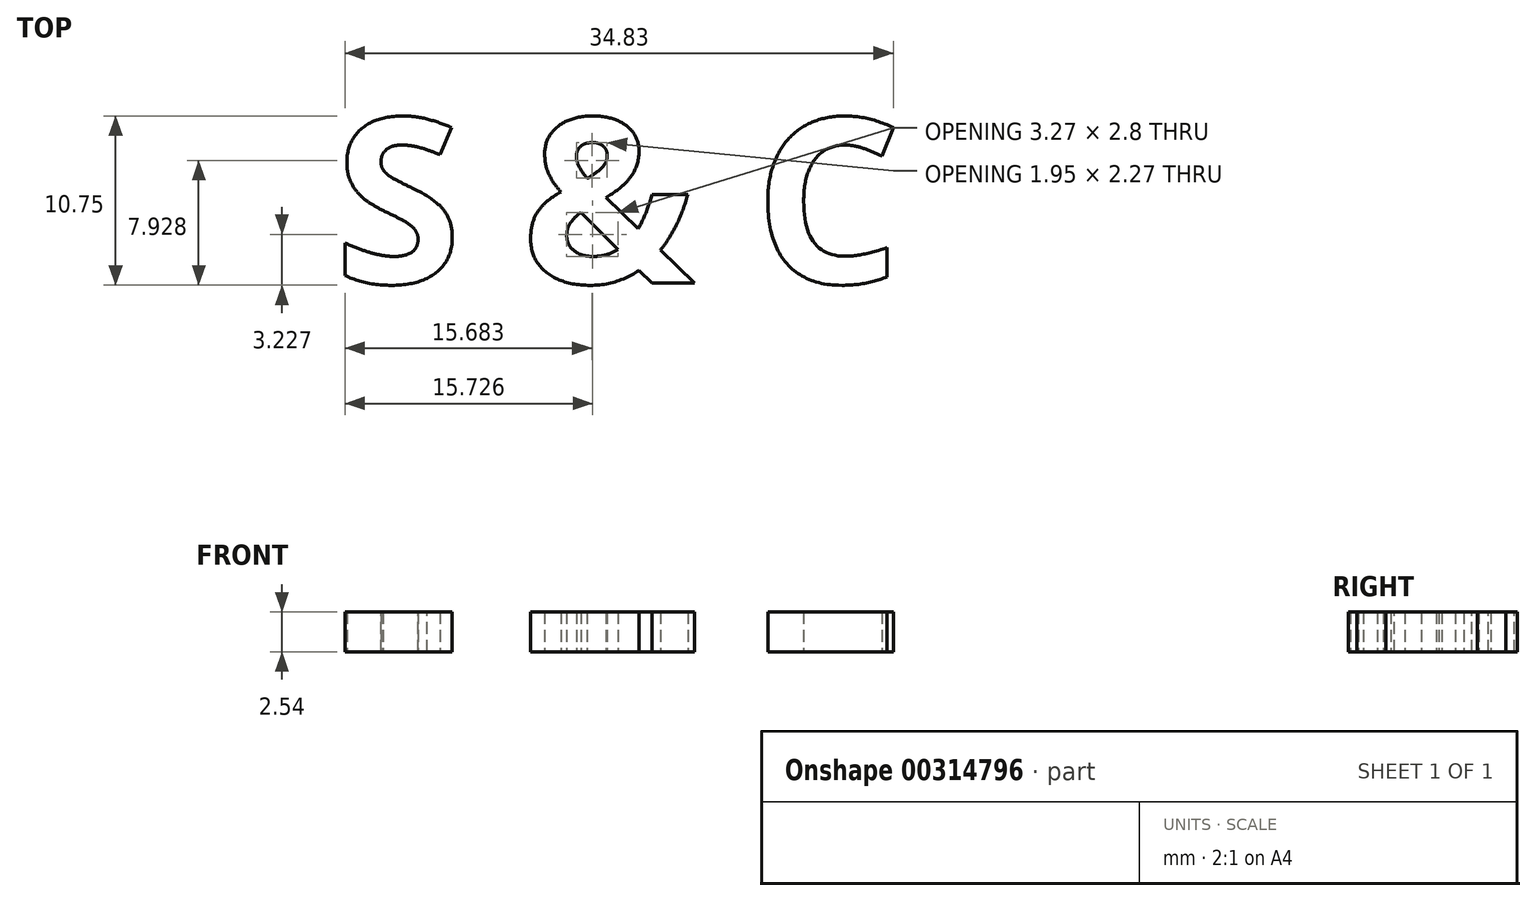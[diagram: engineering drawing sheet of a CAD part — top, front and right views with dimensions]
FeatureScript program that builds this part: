
annotation { "Feature Type Name" : "Feature", "Feature Type Description" : "" }
export const myFeature = defineFeature(function(context is Context, id is Id, definition is map)
    precondition{}
    {
        {
            var Q0;
            Q0=qCreatedBy(makeId("Top.planeOp"),FACE);
            var sketch = newSketch(context, id + "F0", { "sketchPlane" : qUnion([Q0])});
            skText(sketch, "E0", { "text": "S & C", "fontName": "OpenSans-Bold.ttf"});
            const initialGuessF0  = {"E0": [0.06383, 0.06619, 1, 0, 0.01055]};
            skSetInitialGuess(sketch, initialGuessF0);
            skSolve(sketch);
        }
        {
            var Q0;
            Q0=makeQuery(id+"F0.imprint","IMPRINT",FACE,{"disambiguationData":[TD([[makeQuery(id+"F0.imprint","IMPRINT",EDGE,{"derivedFrom":sQuery(id+"F0.wireOp",EDGE,"E0.sketch_text.stroke-62")}),-1.0]])]});
            var Q1;
            Q1=makeQuery(id+"F0.imprint","IMPRINT",FACE,{"disambiguationData":[TD([[makeQuery(id+"F0.imprint","IMPRINT",EDGE,{"derivedFrom":sQuery(id+"F0.wireOp",EDGE,"E0.sketch_text.stroke-28")}),-1.0]])]});
            var Q2;
            Q2=makeQuery(id+"F0.imprint","IMPRINT",FACE,{"disambiguationData":[TD([[makeQuery(id+"F0.imprint","IMPRINT",EDGE,{"derivedFrom":sQuery(id+"F0.wireOp",EDGE,"E0.sketch_text.stroke-0")}),-1.0]])]});
            extrude(context, id + "F1", {"entities" : qUnion([Q0, Q1, Q2]), "depth" : 2.54 * mm});
        }
    });
